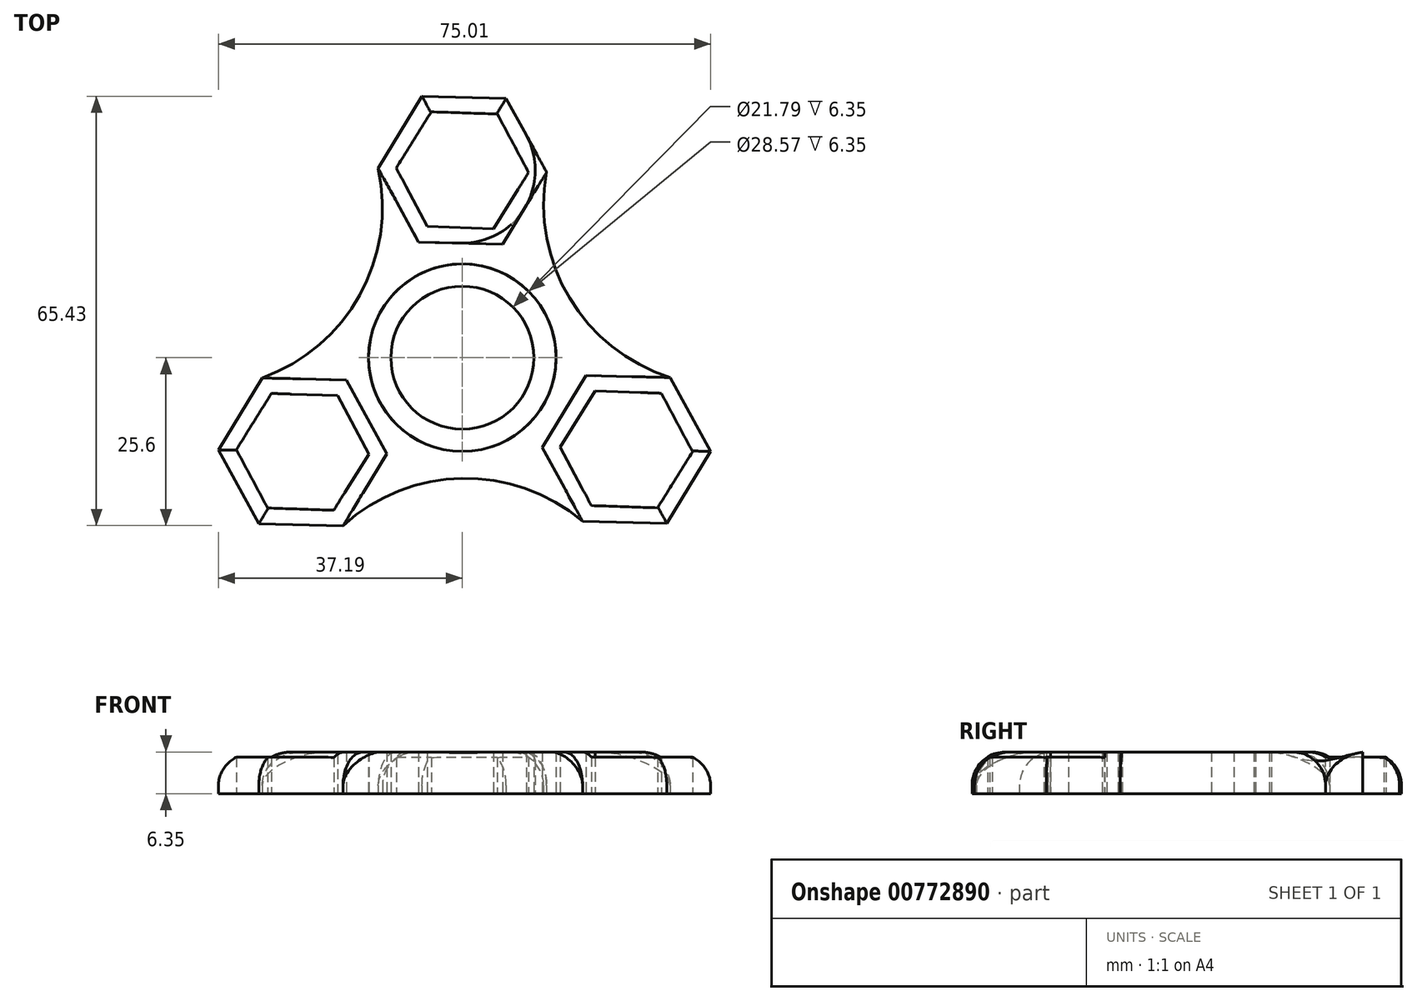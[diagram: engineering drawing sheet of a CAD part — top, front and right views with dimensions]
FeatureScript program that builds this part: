
annotation { "Feature Type Name" : "Feature", "Feature Type Description" : "" }
export const myFeature = defineFeature(function(context is Context, id is Id, definition is map)
    precondition{}
    {
        {
            var Q0;
            Q0=qCreatedBy(makeId("Top.planeOp"),FACE);
            var sketch = newSketch(context, id + "F0", { "sketchPlane" : qUnion([Q0])});
            skCircle(sketch, "E0", {"center": v(0, 0) * mm, "radius": 10.9 * mm});
            skCircle(sketch, "E1", {"center": v(0, 0) * mm, "radius": 14.29 * mm});
            skSolve(sketch);
        }
        {
            var Q0;
            Q0=qCreatedBy(makeId("Top.planeOp"),FACE);
            var sketch = newSketch(context, id + "F1", { "sketchPlane" : qUnion([Q0])});
            skCircle(sketch, "E2.cCircle", {"center": v(0, 28.58) * mm, "radius": 8.74 * mm, "construction": true});
            skLineSegment(sketch, "E2.0", {"start": v(10.08, 28.23) * mm, "end": v(4.75, 19.67) * mm});
            skLineSegment(sketch, "E2.1", {"start": v(4.75, 19.67) * mm, "end": v(-5.34, 20.01) * mm});
            skLineSegment(sketch, "E2.2", {"start": v(-5.34, 20.01) * mm, "end": v(-10.08, 28.92) * mm});
            skLineSegment(sketch, "E2.3", {"start": v(-10.08, 28.92) * mm, "end": v(-4.75, 37.48) * mm});
            skLineSegment(sketch, "E2.4", {"start": v(-4.75, 37.48) * mm, "end": v(5.34, 37.14) * mm});
            skLineSegment(sketch, "E2.5", {"start": v(5.34, 37.14) * mm, "end": v(10.08, 28.23) * mm});
            skPoint(sketch, "E2.0.midPoint", {"position": v(7.42, 23.95) * mm});
            skCircle(sketch, "E3.cCircle", {"center": v(0, 28.58) * mm, "radius": 11.11 * mm, "construction": true});
            skLineSegment(sketch, "E3.0", {"start": v(12.83, 28.28) * mm, "end": v(6.16, 17.32) * mm});
            skLineSegment(sketch, "E3.1", {"start": v(6.16, 17.32) * mm, "end": v(-6.67, 17.61) * mm});
            skLineSegment(sketch, "E3.2", {"start": v(-6.67, 17.61) * mm, "end": v(-12.83, 28.87) * mm});
            skLineSegment(sketch, "E3.3", {"start": v(-12.83, 28.87) * mm, "end": v(-6.16, 39.83) * mm});
            skLineSegment(sketch, "E3.4", {"start": v(-6.16, 39.83) * mm, "end": v(6.67, 39.54) * mm});
            skLineSegment(sketch, "E3.5", {"start": v(6.67, 39.54) * mm, "end": v(12.83, 28.28) * mm});
            skPoint(sketch, "E3.0.midPoint", {"position": v(9.5, 22.8) * mm});
            skCircle(sketch, "E4.1.0", {"center": v(-24.36, -14.35) * mm, "radius": 8.74 * mm, "construction": true});
            skCircle(sketch, "E4.1.1", {"center": v(-24.36, -14.35) * mm, "radius": 11.11 * mm, "construction": true});
            skLineSegment(sketch, "E4.1.2", {"start": v(-37.19, -14.05) * mm, "end": v(-30.52, -3.09) * mm});
            skLineSegment(sketch, "E4.1.3", {"start": v(-17.69, -3.39) * mm, "end": v(-11.53, -14.64) * mm});
            skPoint(sketch, "E4.1.4", {"position": v(-24.06, -5.61) * mm});
            skPoint(sketch, "E4.1.5", {"position": v(-24.1, -3.24) * mm});
            skLineSegment(sketch, "E4.1.6", {"start": v(-31.03, -25.3) * mm, "end": v(-37.19, -14.05) * mm});
            skLineSegment(sketch, "E4.1.7", {"start": v(-29.1, -5.44) * mm, "end": v(-19.02, -5.78) * mm});
            skLineSegment(sketch, "E4.1.8", {"start": v(-19.02, -5.78) * mm, "end": v(-14.28, -14.69) * mm});
            skLineSegment(sketch, "E4.1.9", {"start": v(-14.28, -14.69) * mm, "end": v(-19.61, -23.25) * mm});
            skLineSegment(sketch, "E4.1.10", {"start": v(-19.61, -23.25) * mm, "end": v(-29.7, -22.9) * mm});
            skLineSegment(sketch, "E4.1.11", {"start": v(-29.7, -22.9) * mm, "end": v(-34.44, -14) * mm});
            skLineSegment(sketch, "E4.1.12", {"start": v(-34.44, -14) * mm, "end": v(-29.1, -5.44) * mm});
            skLineSegment(sketch, "E4.1.13", {"start": v(-30.52, -3.09) * mm, "end": v(-17.69, -3.39) * mm});
            skLineSegment(sketch, "E4.1.14", {"start": v(-11.53, -14.64) * mm, "end": v(-18.2, -25.6) * mm});
            skLineSegment(sketch, "E4.1.15", {"start": v(-18.2, -25.6) * mm, "end": v(-31.03, -25.3) * mm});
            skCircle(sketch, "E4.2.0", {"center": v(25, -13.98) * mm, "radius": 8.74 * mm, "construction": true});
            skCircle(sketch, "E4.2.1", {"center": v(25, -13.98) * mm, "radius": 11.11 * mm, "construction": true});
            skLineSegment(sketch, "E4.2.2", {"start": v(31.15, -25.24) * mm, "end": v(18.32, -24.94) * mm});
            skLineSegment(sketch, "E4.2.3", {"start": v(12.16, -13.68) * mm, "end": v(18.83, -2.72) * mm});
            skPoint(sketch, "E4.2.4", {"position": v(17.28, -18.1) * mm});
            skPoint(sketch, "E4.2.5", {"position": v(15.24, -19.31) * mm});
            skLineSegment(sketch, "E4.2.6", {"start": v(37.82, -14.28) * mm, "end": v(31.15, -25.24) * mm});
            skLineSegment(sketch, "E4.2.7", {"start": v(19.65, -22.54) * mm, "end": v(14.9, -13.64) * mm});
            skLineSegment(sketch, "E4.2.8", {"start": v(14.9, -13.64) * mm, "end": v(20.24, -5.08) * mm});
            skLineSegment(sketch, "E4.2.9", {"start": v(20.24, -5.08) * mm, "end": v(30.33, -5.42) * mm});
            skLineSegment(sketch, "E4.2.10", {"start": v(30.33, -5.42) * mm, "end": v(35.07, -14.32) * mm});
            skLineSegment(sketch, "E4.2.11", {"start": v(35.07, -14.32) * mm, "end": v(29.74, -22.88) * mm});
            skLineSegment(sketch, "E4.2.12", {"start": v(29.74, -22.88) * mm, "end": v(19.65, -22.54) * mm});
            skLineSegment(sketch, "E4.2.13", {"start": v(18.32, -24.94) * mm, "end": v(12.16, -13.68) * mm});
            skLineSegment(sketch, "E4.2.14", {"start": v(18.83, -2.72) * mm, "end": v(31.66, -3.02) * mm});
            skLineSegment(sketch, "E4.2.15", {"start": v(31.66, -3.02) * mm, "end": v(37.82, -14.28) * mm});
            skPoint(sketch, "E4.center", {"position": v(0.21, 0.08) * mm});
            skSolve(sketch);
        }
        {
            var Q0;
            Q0=qCreatedBy(makeId("Top.planeOp"),FACE);
            var sketch = newSketch(context, id + "F2", { "sketchPlane" : qUnion([Q0])});
            skLineSegment(sketch, "E5.0", {"start": v(-18.2, -25.6) * mm, "end": v(-31.03, -25.3) * mm});
            skLineSegment(sketch, "E5.1", {"start": v(-30.52, -3.09) * mm, "end": v(-17.69, -3.39) * mm});
            skLineSegment(sketch, "E5.2", {"start": v(31.66, -3.02) * mm, "end": v(37.82, -14.28) * mm});
            skLineSegment(sketch, "E5.3", {"start": v(-29.7, -22.9) * mm, "end": v(-34.44, -14) * mm});
            skLineSegment(sketch, "E5.4", {"start": v(18.32, -24.94) * mm, "end": v(12.16, -13.68) * mm});
            skLineSegment(sketch, "E5.5", {"start": v(29.74, -22.88) * mm, "end": v(19.65, -22.54) * mm});
            skLineSegment(sketch, "E5.6", {"start": v(12.16, -13.68) * mm, "end": v(18.83, -2.72) * mm});
            skLineSegment(sketch, "E5.7", {"start": v(-19.61, -23.25) * mm, "end": v(-29.7, -22.9) * mm});
            skLineSegment(sketch, "E5.8", {"start": v(30.33, -5.42) * mm, "end": v(35.07, -14.32) * mm});
            skCircle(sketch, "E5.9", {"center": v(25, -13.98) * mm, "radius": 11.11 * mm});
            skLineSegment(sketch, "E5.10", {"start": v(-19.02, -5.78) * mm, "end": v(-14.28, -14.69) * mm});
            skLineSegment(sketch, "E5.11", {"start": v(14.9, -13.64) * mm, "end": v(20.24, -5.08) * mm});
            skLineSegment(sketch, "E5.12", {"start": v(-31.03, -25.3) * mm, "end": v(-37.19, -14.05) * mm});
            skLineSegment(sketch, "E5.13", {"start": v(37.82, -14.28) * mm, "end": v(31.15, -25.24) * mm});
            skLineSegment(sketch, "E5.14", {"start": v(-37.19, -14.05) * mm, "end": v(-30.52, -3.09) * mm});
            skCircle(sketch, "E5.15", {"center": v(0, 0) * mm, "radius": 10.9 * mm});
            skCircle(sketch, "E5.16", {"center": v(0, 0) * mm, "radius": 14.29 * mm});
            skLineSegment(sketch, "E5.17", {"start": v(6.67, 39.54) * mm, "end": v(12.83, 28.28) * mm});
            skCircle(sketch, "E5.18", {"center": v(-24.36, -14.35) * mm, "radius": 8.74 * mm});
            skCircle(sketch, "E5.19", {"center": v(-24.36, -14.35) * mm, "radius": 11.11 * mm});
            skCircle(sketch, "E5.20", {"center": v(25, -13.98) * mm, "radius": 8.74 * mm});
            skCircle(sketch, "E5.21", {"center": v(0, 28.58) * mm, "radius": 8.74 * mm});
            skLineSegment(sketch, "E5.22", {"start": v(-11.53, -14.64) * mm, "end": v(-18.2, -25.6) * mm});
            skLineSegment(sketch, "E5.23", {"start": v(4.75, 19.67) * mm, "end": v(-5.34, 20.01) * mm});
            skLineSegment(sketch, "E5.24", {"start": v(-5.34, 20.01) * mm, "end": v(-10.08, 28.92) * mm});
            skLineSegment(sketch, "E5.25", {"start": v(-34.44, -14) * mm, "end": v(-29.1, -5.44) * mm});
            skLineSegment(sketch, "E5.26", {"start": v(-10.08, 28.92) * mm, "end": v(-4.75, 37.48) * mm});
            skLineSegment(sketch, "E5.27", {"start": v(-4.75, 37.48) * mm, "end": v(5.34, 37.14) * mm});
            skLineSegment(sketch, "E5.28", {"start": v(18.83, -2.72) * mm, "end": v(31.66, -3.02) * mm});
            skLineSegment(sketch, "E5.29", {"start": v(5.34, 37.14) * mm, "end": v(10.08, 28.23) * mm});
            skCircle(sketch, "E5.30", {"center": v(0, 28.58) * mm, "radius": 11.11 * mm});
            skLineSegment(sketch, "E5.31", {"start": v(35.07, -14.32) * mm, "end": v(29.74, -22.88) * mm});
            skLineSegment(sketch, "E5.32", {"start": v(31.15, -25.24) * mm, "end": v(18.32, -24.94) * mm});
            skLineSegment(sketch, "E5.33", {"start": v(-14.28, -14.69) * mm, "end": v(-19.61, -23.25) * mm});
            skLineSegment(sketch, "E5.34", {"start": v(6.16, 17.32) * mm, "end": v(-6.67, 17.61) * mm});
            skLineSegment(sketch, "E5.35", {"start": v(20.24, -5.08) * mm, "end": v(30.33, -5.42) * mm});
            skLineSegment(sketch, "E5.36", {"start": v(-6.67, 17.61) * mm, "end": v(-12.83, 28.87) * mm});
            skLineSegment(sketch, "E5.37", {"start": v(-12.83, 28.87) * mm, "end": v(-6.16, 39.83) * mm});
            skLineSegment(sketch, "E5.38", {"start": v(-17.69, -3.39) * mm, "end": v(-11.53, -14.64) * mm});
            skLineSegment(sketch, "E5.39", {"start": v(-6.16, 39.83) * mm, "end": v(6.67, 39.54) * mm});
            skLineSegment(sketch, "E5.40", {"start": v(10.08, 28.23) * mm, "end": v(4.75, 19.67) * mm});
            skLineSegment(sketch, "E5.41", {"start": v(19.65, -22.54) * mm, "end": v(14.9, -13.64) * mm});
            skArc(sketch, "E6", {"start": v(-30.52, -3.09) * mm, "mid": v(-15.64, 9.55) * mm, "end": v(-12.83, 28.87) * mm});
            skArc(sketch, "E7", {"start": v(18.32, -24.94) * mm, "mid": v(-0.07, -18.38) * mm, "end": v(-18.2, -25.6) * mm});
            skArc(sketch, "E8", {"start": v(12.83, 28.28) * mm, "mid": v(16.34, 9.07) * mm, "end": v(31.66, -3.02) * mm});
            skSolve(sketch);
        }
        {
            var Q0;
            Q0=makeQuery(id+"F2.imprint","IMPRINT",FACE,{"disambiguationData":[TD([[makeQuery(id+"F2.imprint","IMPRINT",EDGE,{"derivedFrom":sQuery(id+"F2.wireOp",EDGE,"E5.16")}),-1.0]])]});
            var Q1;
            Q1=makeQuery(id+"F1.imprint","IMPRINT",FACE,{"disambiguationData":[TD([[makeQuery(id+"F1.imprint","IMPRINT",EDGE,{"derivedFrom":sQuery(id+"F1.wireOp",EDGE,"E4.1.2")}),-1.0]])]});
            var Q2;
            Q2=makeQuery(id+"F0.imprint","IMPRINT",FACE,{"disambiguationData":[TD([[makeQuery(id+"F0.imprint","IMPRINT",EDGE,{"derivedFrom":sQuery(id+"F0.wireOp",EDGE,"E0")}),-1.0]])]});
            var Q3;
            Q3=makeQuery(id+"F1.imprint","IMPRINT",FACE,{"disambiguationData":[TD([[makeQuery(id+"F1.imprint","IMPRINT",EDGE,{"derivedFrom":sQuery(id+"F1.wireOp",EDGE,"E2.0")}),1.0]])]});
            var Q4;
            Q4=makeQuery(id+"F1.imprint","IMPRINT",FACE,{"disambiguationData":[TD([[makeQuery(id+"F1.imprint","IMPRINT",EDGE,{"derivedFrom":sQuery(id+"F1.wireOp",EDGE,"E4.2.2")}),-1.0]])]});
            extrude(context, id + "F3", {"entities" : qUnion([Q0, Q1, Q2, Q3, Q4]), "depth" : 6.35 * mm, "offsetDistance" : 25.4 * mm});
        }
        {
            var Q0;
            Q0=makeQuery(id+"F3.opExtrude","CAP_EDGE",EDGE,{"disambiguationData":[OSD([sQuery(id+"F1.wireOp",EDGE,"E4.1.2")])],"isStart":false});
            var Q1;
            Q1=makeQuery(id+"F3.opExtrude","CAP_EDGE",EDGE,{"disambiguationData":[OSD([sQuery(id+"F1.wireOp",EDGE,"E3.3")])],"isStart":false});
            var Q2;
            Q2=makeQuery(id+"F3.opExtrude","CAP_EDGE",EDGE,{"disambiguationData":[OSD([sQuery(id+"F1.wireOp",EDGE,"E3.4")])],"isStart":false});
            var Q3;
            Q3=makeQuery(id+"F3.opExtrude","CAP_EDGE",EDGE,{"disambiguationData":[OSD([sQuery(id+"F1.wireOp",EDGE,"E3.5")])],"isStart":false});
            var Q4;
            Q4=makeQuery(id+"F3.opExtrude","CAP_EDGE",EDGE,{"disambiguationData":[OSD([sQuery(id+"F2.wireOp",EDGE,"E6")])],"isStart":false});
            var Q5;
            Q5=makeQuery(id+"F3.opExtrude","CAP_EDGE",EDGE,{"disambiguationData":[OSD([sQuery(id+"F1.wireOp",EDGE,"E4.1.6")])],"isStart":false});
            var Q6;
            Q6=makeQuery(id+"F3.opExtrude","CAP_EDGE",EDGE,{"disambiguationData":[OSD([sQuery(id+"F1.wireOp",EDGE,"E4.1.15")])],"isStart":false});
            var Q7;
            Q7=makeQuery(id+"F3.opExtrude","CAP_EDGE",EDGE,{"disambiguationData":[OSD([sQuery(id+"F2.wireOp",EDGE,"E7")])],"isStart":false});
            var Q8;
            Q8=makeQuery(id+"F3.opExtrude","CAP_EDGE",EDGE,{"disambiguationData":[OSD([sQuery(id+"F1.wireOp",EDGE,"E4.2.2")])],"isStart":false});
            var Q9;
            Q9=makeQuery(id+"F3.opExtrude","CAP_EDGE",EDGE,{"disambiguationData":[OSD([sQuery(id+"F1.wireOp",EDGE,"E4.2.6")])],"isStart":false});
            var Q10;
            Q10=makeQuery(id+"F3.opExtrude","CAP_EDGE",EDGE,{"disambiguationData":[OSD([sQuery(id+"F1.wireOp",EDGE,"E4.2.15")])],"isStart":false});
            var Q11;
            Q11=makeQuery(id+"F3.opExtrude","CAP_EDGE",EDGE,{"disambiguationData":[OSD([sQuery(id+"F2.wireOp",EDGE,"E8")])],"isStart":false});
            fillet(context, id + "F4", {"entities" : qUnion([Q0, Q1, Q2, Q3, Q4, Q5, Q6, Q7, Q8, Q9, Q10, Q11]), "radius" : 5.08 * mm, "tangentPropagation" : true, "allowEdgeOverflow" : false});
        }
    });
